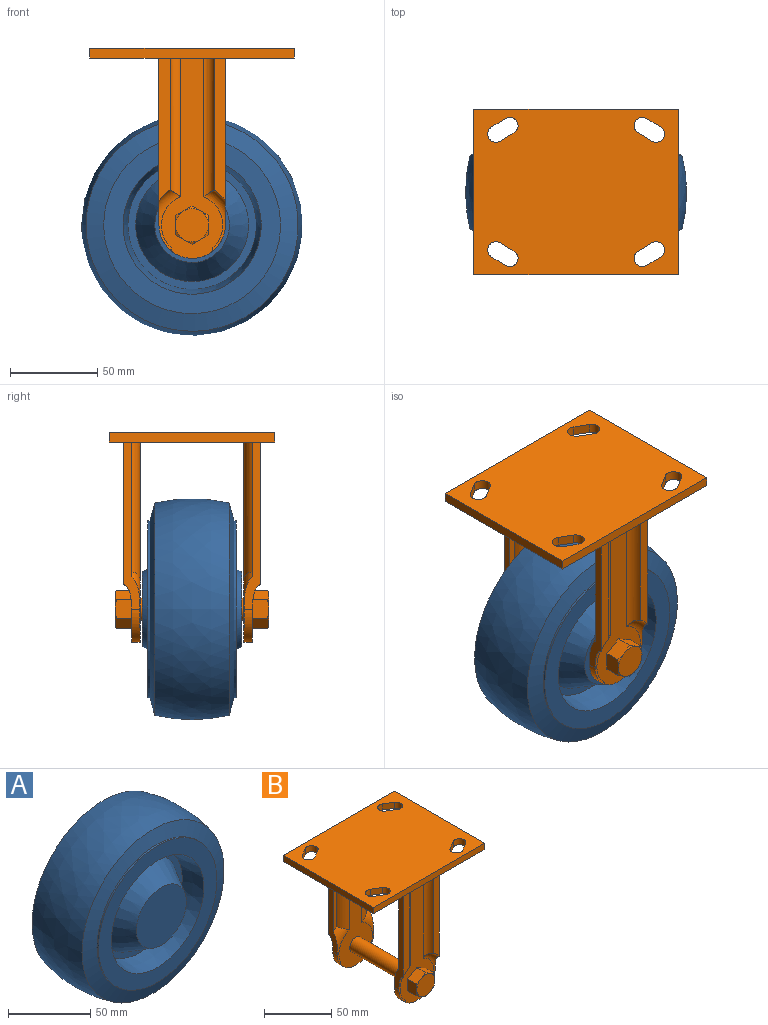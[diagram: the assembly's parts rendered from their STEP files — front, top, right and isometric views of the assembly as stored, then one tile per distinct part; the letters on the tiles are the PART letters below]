
ASSEMBLY  parts=2 mates=1
PART A: 15 faces, bbox 127x57.2x127 mm
  f0: cone r=21.43mm half-angle=30deg, axis (0,-1,0), area 3722.1mm2, adj f13,f14
  f1: cone r=36.89mm half-angle=10deg, axis (0,1,0), area 3878mm2, adj f12,f13
  f2: cylinder r=50.8mm len=101.6mm, axis (0,1,0), area 405.4mm2, adj f3,f12
  f3: cone r=50.8mm half-angle=75deg, axis (0,-1,0), area 3693.1mm2, adj f2,f4
  f4: revolved ~127x127mm, area 17012.1mm2, adj f3,f5
  f5: cone r=60.96mm half-angle=75deg, axis (0,1,0), area 3693.1mm2, adj f4,f6
  f6: cylinder r=50.8mm len=101.6mm, axis (0,1,0), area 405.4mm2, adj f5,f11
  f7: cone r=39.69mm half-angle=10deg, axis (0,-1,0), area 3878mm2, adj f10,f11
  f8: cone r=32.43mm half-angle=30deg, axis (0,1,0), area 3722.1mm2, adj f9,f10
  f9: plane 42.86x42.86mm, normal (0,-1,0), area 1442.9mm2, adj f8
  f10: plane 73.78x73.78mm, normal (0,-1,0), area 970.9mm2, adj f7,f8
  f11: plane 101.6x101.6mm, normal (0,-1,0), area 3159mm2, adj f6,f7
  f12: plane 101.6x101.6mm, normal (0,1,0), area 3159mm2, adj f1,f2
  f13: plane 73.78x73.78mm, normal (0,1,0), area 970.9mm2, adj f0,f1
  f14: plane 42.86x42.86mm, normal (0,1,0), area 1442.9mm2, adj f0
PART B: 91 faces, bbox 118.4x96.2x122.8 mm
  f0: cylinder r=4.76mm len=8.85mm, axis (0,0,1), area 83.1mm2, adj f73,f78,f88,f90
  f1: cylinder r=4.76mm len=8.85mm, axis (0,0,1), area 83.1mm2, adj f73,f78,f85,f87
  f2: cylinder r=4.76mm len=8.85mm, axis (0,0,1), area 83.1mm2, adj f73,f78,f83,f84
  f3: cylinder r=4.76mm len=8.85mm, axis (0,0,1), area 83.1mm2, adj f73,f78,f80,f81
  f4: cylinder r=6.35mm len=59.69mm, axis (0,1,0), area 2381.5mm2, adj f25,f26
  f5: torus R=17.66mm, axis (0,1,0), area 141.9mm2, adj f10,f27,f45,f49,f51,f59
  f6: torus R=17.66mm, axis (0,-1,0), area 141.9mm2, adj f9,f11,f44,f48,f53,f56
  f7: torus R=17.66mm, axis (0,1,0), area 142.3mm2, adj f10,f26,f31,f37,f38,f45
  f8: torus R=17.66mm, axis (0,-1,0), area 142.3mm2, adj f9,f25,f28,f33,f40,f44
  f9: plane 96.05x9.44mm, normal (1,0,0), area 472.7mm2, adj f6,f8,f40,f44,f48,f73
  f10: plane 96.05x9.44mm, normal (-1,0,0), area 472.9mm2, adj f5,f7,f38,f45,f49,f73
  f11: plane 115.09x35.33mm, normal (0,1,0), area 1734.2mm2, adj f6,f44,f46,f53,f54,f56,f57,f60
  f12: plane 10.43x10.43mm, normal (-0.5,0,-0.87), area 101.6mm2, adj f13,f17,f19,f20,f27
  f13: plane 10.43x10.43mm, normal (0.5,0,-0.87), area 101.6mm2, adj f12,f14,f18,f19,f27
  f14: plane 11.91x10.43mm, normal (1,0,0), area 101.6mm2, adj f13,f15,f18,f23,f27
  f15: plane 10.43x10.43mm, normal (0.5,0,0.87), area 101.5mm2, adj f14,f16,f22,f23,f27
  f16: plane 10.43x10.43mm, normal (-0.5,0,0.87), area 101.6mm2, adj f15,f17,f21,f22,f27
  f17: plane 11.91x10.43mm, normal (-1,0,0), area 101.6mm2, adj f12,f16,f20,f21,f27
  f18: cone r=9.53mm half-angle=60deg, axis (0,1,0), area 8.9mm2, adj f13,f14,f24
  f19: cone r=9.53mm half-angle=60deg, axis (0,1,0), area 8.9mm2, adj f12,f13,f24
  f20: cone r=9.53mm half-angle=60deg, axis (0,1,0), area 8.9mm2, adj f12,f17,f24
  f21: cone r=9.53mm half-angle=60deg, axis (0,1,0), area 8.9mm2, adj f16,f17,f24
  f22: cone r=9.53mm half-angle=60deg, axis (0,1,0), area 8.9mm2, adj f15,f16,f24
  f23: cone r=9.53mm half-angle=60deg, axis (0,1,0), area 8.9mm2, adj f14,f15,f24
  f24: plane 19.05x19.05mm, normal (0,-1,0), area 285mm2, adj f18,f19,f20,f21,f22,f23
  f25: plane 115.09x35.33mm, normal (0,-1,0), area 1939.1mm2, adj f4,f8,f28,f29,f32,f33,f39,f44
  f26: plane 115.09x35.33mm, normal (0,1,0), area 1939.1mm2, adj f4,f7,f30,f31,f35,f36,f37,f45
  f27: plane 115.09x35.33mm, normal (0,-1,0), area 1734.2mm2, adj f5,f12,f13,f14,f15,f16,f17,f45
  f28: cylinder r=11.11mm len=79.64mm, axis (0,0,-1), area 823.4mm2, adj f8,f25,f40,f73
  f29: cylinder r=11.11mm len=79.64mm, axis (0,0,1), area 823.4mm2, adj f25,f32,f34,f73
  f30: cylinder r=11.11mm len=79.64mm, axis (0,0,-1), area 823.4mm2, adj f26,f35,f41,f73
  f31: cylinder r=11.11mm len=79.64mm, axis (0,0,1), area 823.4mm2, adj f7,f26,f38,f73
  f32: torus R=17.66mm, axis (0,-1,0), area 142.3mm2, adj f25,f29,f34,f39,f43,f44
  f33: plane 3x0.31mm, normal (0.98,-0.17,0), area 0.1mm2, adj f8,f25,f44
  f34: plane 77.22x3.38mm, normal (0,-1,0), area 255.7mm2, adj f29,f32,f43,f73
  f35: torus R=17.66mm, axis (0,1,0), area 142.3mm2, adj f26,f30,f36,f41,f42,f45
  f36: plane 3x0.31mm, normal (0.98,0.17,0), area 0.1mm2, adj f26,f35,f45
  f37: plane 3x0.31mm, normal (-0.98,0.17,0), area 0.1mm2, adj f7,f26,f45
  f38: plane 77.22x3.38mm, normal (0,1,0), area 255.7mm2, adj f7,f10,f31,f73
  f39: plane 3x0.31mm, normal (-0.98,-0.17,0), area 0.1mm2, adj f25,f32,f44
  f40: plane 77.22x3.38mm, normal (0,-1,0), area 255.7mm2, adj f8,f9,f28,f73
  f41: plane 77.22x3.38mm, normal (0,1,0), area 255.7mm2, adj f30,f35,f42,f73
  f42: plane 96.05x9.44mm, normal (1,0,0), area 472.7mm2, adj f35,f41,f45,f50,f55,f73
  f43: plane 96.05x9.44mm, normal (-1,0,0), area 472.6mm2, adj f32,f34,f44,f47,f54,f73
  f44: cylinder r=19.05mm len=38.1mm, axis (0,1,0), area 288.3mm2, adj f6,f8,f9,f11,f25,f32,f33,f39
  f45: cylinder r=19.05mm len=38.1mm, axis (0,1,0), area 288.3mm2, adj f5,f7,f10,f26,f27,f35,f36,f37
  f46: plane 1.9x0.23mm, normal (0.98,0.17,0), area 0.1mm2, adj f11,f44,f54
  f47: plane 81.76x6.35mm, normal (0,1,0), area 498.3mm2, adj f43,f54,f57,f73
  f48: plane 81.76x6.35mm, normal (0,1,0), area 498.3mm2, adj f6,f9,f56,f73
  f49: plane 81.76x6.35mm, normal (0,-1,0), area 498.3mm2, adj f5,f10,f59,f73
  f50: plane 81.76x6.35mm, normal (0,-1,0), area 498.3mm2, adj f42,f55,f58,f73
  f51: plane 1.9x0.23mm, normal (0.98,-0.17,0), area 0.1mm2, adj f5,f27,f45
  f52: plane 1.9x0.23mm, normal (-0.98,-0.17,0), area 0.1mm2, adj f27,f45,f55
  f53: plane 1.9x0.23mm, normal (-0.98,0.17,0), area 0.1mm2, adj f6,f11,f44
  f54: torus R=17.66mm, axis (0,-1,0), area 141.9mm2, adj f11,f43,f44,f46,f47,f57
  f55: torus R=17.66mm, axis (0,1,0), area 141.9mm2, adj f27,f42,f45,f50,f52,f58
  f56: cylinder r=6.35mm len=79.64mm, axis (0,0,-1), area 650.9mm2, adj f6,f11,f48,f73
  f57: cylinder r=6.35mm len=79.64mm, axis (0,0,1), area 650.9mm2, adj f11,f47,f54,f73
  f58: cylinder r=6.35mm len=79.64mm, axis (0,0,-1), area 650.9mm2, adj f27,f50,f55,f73
  f59: cylinder r=6.35mm len=79.64mm, axis (0,0,1), area 650.9mm2, adj f5,f27,f49,f73
  f60: plane 10.43x10.43mm, normal (-0.5,0,-0.87), area 101.6mm2, adj f11,f61,f65,f67,f68
  f61: plane 10.43x10.43mm, normal (0.5,0,-0.87), area 101.6mm2, adj f11,f60,f62,f66,f67
  f62: plane 11.91x10.43mm, normal (1,0,0), area 101.6mm2, adj f11,f61,f63,f66,f71
  f63: plane 10.43x10.43mm, normal (0.5,0,0.87), area 101.5mm2, adj f11,f62,f64,f70,f71
  f64: plane 10.43x10.43mm, normal (-0.5,0,0.87), area 101.6mm2, adj f11,f63,f65,f69,f70
  f65: plane 11.91x10.43mm, normal (-1,0,0), area 101.6mm2, adj f11,f60,f64,f68,f69
  f66: cone r=9.53mm half-angle=60deg, axis (0,-1,0), area 8.9mm2, adj f61,f62,f72
  f67: cone r=9.53mm half-angle=60deg, axis (0,-1,0), area 8.9mm2, adj f60,f61,f72
  f68: cone r=9.53mm half-angle=60deg, axis (0,-1,0), area 8.9mm2, adj f60,f65,f72
  f69: cone r=9.53mm half-angle=60deg, axis (0,-1,0), area 8.9mm2, adj f64,f65,f72
  f70: cone r=9.53mm half-angle=60deg, axis (0,-1,0), area 8.9mm2, adj f63,f64,f72
  f71: cone r=9.53mm half-angle=60deg, axis (0,-1,0), area 8.9mm2, adj f62,f63,f72
  f72: plane 19.05x19.05mm, normal (0,1,0), area 285mm2, adj f66,f67,f68,f69,f70,f71
  f73: plane 117.48x95.25mm, normal (0,0,-1), area 10153.8mm2, adj f0,f1,f2,f3,f9,f10,f11,f25
  f74: plane 95.25x5.56mm, normal (-1,0,0), area 529.2mm2, adj f73,f75,f77,f78
  f75: plane 117.48x5.56mm, normal (0,1,0), area 652.7mm2, adj f73,f74,f76,f78
  f76: plane 95.25x5.56mm, normal (1,0,0), area 529.2mm2, adj f73,f75,f77,f78
  f77: plane 117.48x5.56mm, normal (0,-1,0), area 652.7mm2, adj f73,f74,f76,f78
  f78: plane 117.48x95.25mm, normal (0,0,1), area 10551.8mm2, adj f0,f1,f2,f3,f74,f75,f76,f77
  f79: cylinder r=4.76mm len=8.85mm, axis (0,0,1), area 83.1mm2, adj f73,f78,f80,f81
  f80: plane 7.94x5.56mm, normal (-0.51,-0.86,0), area 51.4mm2, adj f3,f73,f78,f79
  f81: plane 7.94x5.56mm, normal (0.51,0.86,0), area 51.4mm2, adj f3,f73,f78,f79
  f82: cylinder r=4.76mm len=8.85mm, axis (0,0,1), area 83.1mm2, adj f73,f78,f83,f84
  f83: plane 7.94x5.56mm, normal (-0.51,0.86,0), area 51.4mm2, adj f2,f73,f78,f82
  f84: plane 7.94x5.56mm, normal (0.51,-0.86,0), area 51.4mm2, adj f2,f73,f78,f82
  f85: plane 7.94x5.56mm, normal (0.51,-0.86,0), area 51.4mm2, adj f1,f73,f78,f86
  f86: cylinder r=4.76mm len=8.85mm, axis (0,0,1), area 83.1mm2, adj f73,f78,f85,f87
  f87: plane 7.94x5.56mm, normal (-0.51,0.86,0), area 51.4mm2, adj f1,f73,f78,f86
  f88: plane 7.94x5.56mm, normal (0.51,0.86,0), area 51.4mm2, adj f0,f73,f78,f89
  f89: cylinder r=4.76mm len=8.85mm, axis (0,0,1), area 83.1mm2, adj f73,f78,f88,f90
  f90: plane 7.94x5.56mm, normal (-0.51,-0.86,0), area 51.4mm2, adj f0,f73,f78,f89
PLACE A at identity
PLACE B at identity
MATE fastened A.f0 <-> B.f4  axis (0,1,0) through (0,28.58,-101.6)mm
